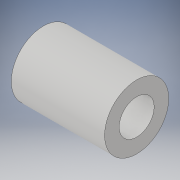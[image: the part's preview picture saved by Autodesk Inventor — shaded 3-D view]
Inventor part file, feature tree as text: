
AUTODESK INVENTOR PART (.ipt)
format: ipt  version: 2017 (Build 210142000, 142)  size: 97,792 bytes
history: native  units: in
note: dims shown in document units (in); Inventor stores cm internally (conversion verified against a paired STEP export)
features: extrude x2, sketch x2
ambient origin geometry x8: Origin, YZ Plane, XZ Plane, XY Plane, X Axis, Y Axis, Z Axis, Center Point
bodies: Solid1 (feature_tree)
feature tree (4):
  extrude  "Extrusion1"  Depth=1.2598in TaperAngle=0.0deg
  extrude  "Extrusion2"  Depth=1.2598in TaperAngle=0.0deg
  sketch  "Sketch1"  dims[d0=0.8661in d1=1.2598in d2=0.0in]
  sketch  "Sketch2"  dims[d3=0.4724in d4=1.2598in d5=0.0in]
